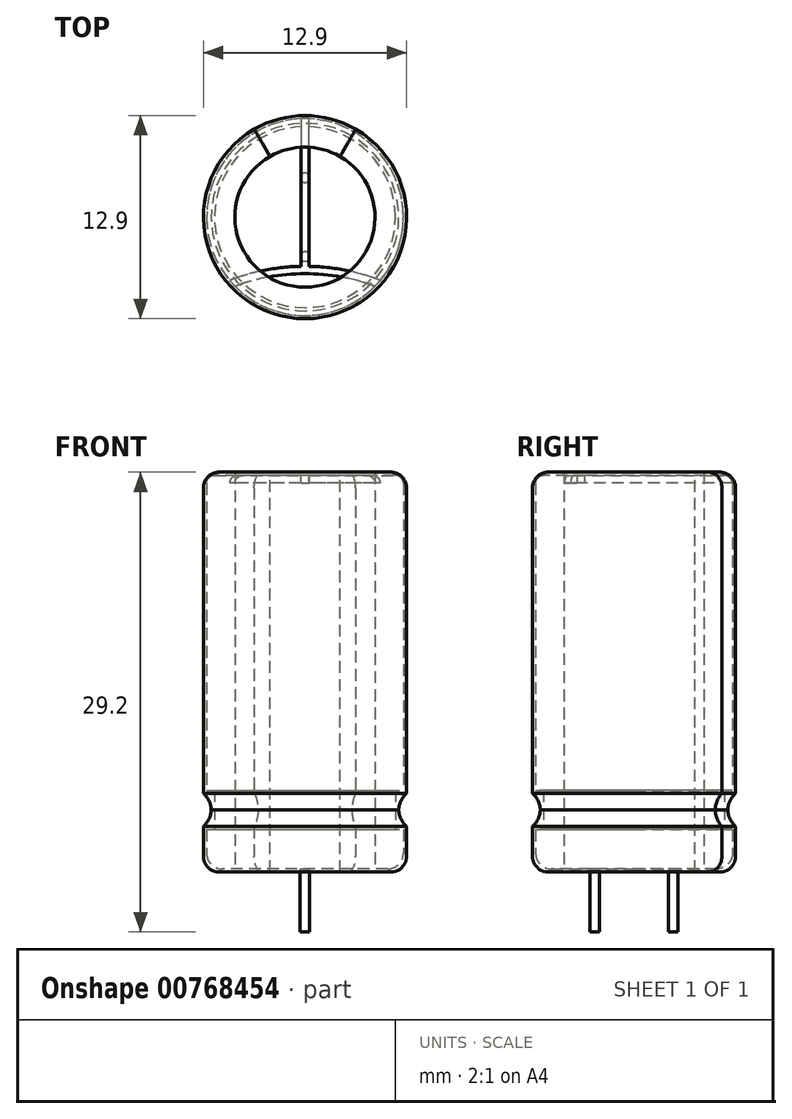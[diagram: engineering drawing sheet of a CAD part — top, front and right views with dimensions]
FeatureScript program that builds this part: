
annotation { "Feature Type Name" : "Feature", "Feature Type Description" : "" }
export const myFeature = defineFeature(function(context is Context, id is Id, definition is map)
    precondition{}
    {
        {
            var Q0;
            Q0=qCreatedBy(makeId("Front.planeOp"),FACE);
            var sketch = newSketch(context, id + "F0", { "sketchPlane" : qUnion([Q0])});
            skLineSegment(sketch, "E0", {"start": v(0, 0) * mm, "end": v(0, 25) * mm});
            skLineSegment(sketch, "E1", {"start": v(0, 25) * mm, "end": v(6.25, 25) * mm});
            skLineSegment(sketch, "E2", {"start": v(6.25, 25) * mm, "end": v(6.25, 5) * mm});
            skLineSegment(sketch, "E3", {"start": v(6.25, 5) * mm, "end": v(5.75, 5) * mm});
            skLineSegment(sketch, "E4", {"start": v(5.75, 5) * mm, "end": v(5.75, 2.5) * mm});
            skLineSegment(sketch, "E5", {"start": v(5.75, 2.5) * mm, "end": v(6.25, 2.5) * mm});
            skLineSegment(sketch, "E6", {"start": v(6.25, 2.5) * mm, "end": v(6.25, 0) * mm});
            skLineSegment(sketch, "E7", {"start": v(6.25, 0) * mm, "end": v(0, 0) * mm});
            skSolve(sketch);
        }
        {
            var Q0;
            Q0=makeQuery(id+"F0.imprint","IMPRINT",FACE,{"disambiguationData":[TD([[makeQuery(id+"F0.imprint","IMPRINT",EDGE,{"derivedFrom":sQuery(id+"F0.wireOp",EDGE,"E0")}),-1.0]])]});
            var Q1;
            Q1=sQuery(id+"F0.wireOp",EDGE,"E0");
            revolve(context, id + "F1", {"surfaceOperationType" : NewSurfaceOperationType.NEW, "entities" : qUnion([Q0]), "axis" : qUnion([Q1]), "revolveType" : RevolveType.FULL});
        }
        {
            var Q0;
            Q0=makeQuery(id+"F1.opRevolve","SWEPT_FACE",FACE,{"disambiguationData":[OSD([sQuery(id+"F0.wireOp",EDGE,"E1")])]});
            var sketch = newSketch(context, id + "F2", { "sketchPlane" : qUnion([Q0])});
            skLineSegment(sketch, "E8", {"start": v(0, 0) * mm, "end": v(-4.79, -4.02) * mm, "construction": true});
            skLineSegment(sketch, "E9", {"start": v(0, 0) * mm, "end": v(4.79, -4.02) * mm, "construction": true});
            skArc(sketch, "E10", {"start": v(4.79, -4.02) * mm, "mid": v(0, -3.12) * mm, "end": v(-4.79, -4.02) * mm});
            skLineSegment(sketch, "E11", {"start": v(-0.25, 6.24) * mm, "end": v(-0.25, -3.13) * mm});
            skLineSegment(sketch, "E12", {"start": v(0.25, -3.13) * mm, "end": v(0.25, 6.24) * mm});
            skArc(sketch, "E13", {"start": v(4.45, -4.39) * mm, "mid": v(0, -3.59) * mm, "end": v(-4.45, -4.39) * mm});
            skSolve(sketch);
        }
        {
            var Q0;
            {var subQ0=sQuery(id+"F2.wireOp",EDGE,"E11");Q0=makeQuery(id+"F2.imprint","IMPRINT",FACE,{"disambiguationData":[TD([[makeQuery(id+"F2.imprint","IMPRINT",EDGE,{"derivedFrom":subQ0}),1.0]])]});}
            var Q1;
            {var subQ5=sQuery(id+"F2.wireOp",EDGE,"E13");Q1=makeQuery(id+"F2.imprint","IMPRINT",FACE,{"disambiguationData":[TD([[makeQuery(id+"F2.imprint","IMPRINT",EDGE,{"derivedFrom":subQ5}),-1.0]])]});}
            extrude(context, id + "F3", {"entities" : qUnion([Q0, Q1]), "operationType" : NewBodyOperationType.REMOVE, "oppositeDirection" : true, "depth" : 0.5 * mm, "offsetDistance" : 25 * mm});
        }
        {
            var Q0;
            {var subQ0=sQuery(id+"F0.wireOp",EDGE,"E1");var subQ1=sQuery(id+"F0.wireOp",EDGE,"E2");var subQ3=makeQuery(id+"F1.opRevolve","SWEPT_EDGE",EDGE,{"disambiguationData":[OSD([subQ0,subQ1])]});var subQ4=sQuery(id+"F2.wireOp",EDGE,"E11");Q0=makeQuery(id+"F3.boolean.opBoolean","SPLIT",EDGE,{"disambiguationData":[TD([makeQuery(id+"F3.opExtrude","SWEPT_FACE",FACE,{"disambiguationData":[OSD([subQ4])]})])],"derivedFrom":subQ3});}
            var Q1;
            {var subQ0=sQuery(id+"F0.wireOp",EDGE,"E1");var subQ1=sQuery(id+"F0.wireOp",EDGE,"E2");Q1=makeQuery(id+"F3.boolean.opBoolean","SPLIT",EDGE,{"disambiguationData":[TD([makeQuery(id+"F3.opExtrude","SWEPT_FACE",FACE,{"disambiguationData":[OSD([sQuery(id+"F2.wireOp",EDGE,"E13")])]})])],"derivedFrom":makeQuery(id+"F1.opRevolve","SWEPT_EDGE",EDGE,{"disambiguationData":[OSD([subQ0,subQ1])]})});}
            var Q2;
            {var subQ0=sQuery(id+"F0.wireOp",EDGE,"E1");var subQ1=sQuery(id+"F0.wireOp",EDGE,"E2");var subQ3=makeQuery(id+"F1.opRevolve","SWEPT_EDGE",EDGE,{"disambiguationData":[OSD([subQ0,subQ1])]});var subQ4=sQuery(id+"F2.wireOp",EDGE,"E12");Q2=makeQuery(id+"F3.boolean.opBoolean","SPLIT",EDGE,{"disambiguationData":[TD([makeQuery(id+"F3.opExtrude","SWEPT_FACE",FACE,{"disambiguationData":[OSD([subQ4])]})])],"derivedFrom":subQ3});}
            fillet(context, id + "F4", {"entities" : qUnion([Q0, Q1, Q2]), "radius" : 0.5 * mm, "tangentPropagation" : true, "allowEdgeOverflow" : false});
        }
        {
            var Q0;
            Q0=makeQuery(id+"F1.opRevolve","SWEPT_EDGE",EDGE,{"disambiguationData":[OSD([sQuery(id+"F0.wireOp",EDGE,"E6"),sQuery(id+"F0.wireOp",EDGE,"E7")])]});
            fillet(context, id + "F5", {"entities" : qUnion([Q0]), "radius" : 1 * mm, "tangentPropagation" : true, "allowEdgeOverflow" : false});
        }
        {
            var Q0;
            Q0=qCreatedBy(makeId("Front.planeOp"),FACE);
            var sketch = newSketch(context, id + "F6", { "sketchPlane" : qUnion([Q0])});
            skLineSegment(sketch, "E14.0", {"start": v(6.25, 0) * mm, "end": v(0, 0) * mm, "construction": true});
            skLineSegment(sketch, "E15.0", {"start": v(6.25, 2.5) * mm, "end": v(6.25, 0) * mm, "construction": true});
            skLineSegment(sketch, "E16.0", {"start": v(5.75, 2.5) * mm, "end": v(6.25, 2.5) * mm, "construction": true});
            skLineSegment(sketch, "E17", {"start": v(5.75, 5) * mm, "end": v(5.75, 2.5) * mm, "construction": true});
            skLineSegment(sketch, "E18.0", {"start": v(6.25, 5) * mm, "end": v(5.75, 5) * mm, "construction": true});
            skLineSegment(sketch, "E19.0", {"start": v(6.25, 25) * mm, "end": v(6.25, 5) * mm, "construction": true});
            skLineSegment(sketch, "E20.0", {"start": v(6.45, 2.7) * mm, "end": v(6.45, 0) * mm});
            skLineSegment(sketch, "E20.1", {"start": v(6.45, 25) * mm, "end": v(6.45, 4.8) * mm});
            skLineSegment(sketch, "E20.2", {"start": v(6.45, 4.8) * mm, "end": v(5.95, 4.8) * mm});
            skLineSegment(sketch, "E20.3", {"start": v(5.95, 4.8) * mm, "end": v(5.95, 2.7) * mm});
            skLineSegment(sketch, "E20.4", {"start": v(5.95, 2.7) * mm, "end": v(6.45, 2.7) * mm});
            skLineSegment(sketch, "E21", {"start": v(6.45, 0) * mm, "end": v(6.45, -0.2) * mm});
            skLineSegment(sketch, "E22", {"start": v(6.45, -0.2) * mm, "end": v(4.45, -0.2) * mm});
            skLineSegment(sketch, "E23", {"start": v(4.45, -0.2) * mm, "end": v(4.45, 25.2) * mm});
            skLineSegment(sketch, "E24", {"start": v(4.45, 25.2) * mm, "end": v(6.45, 25.2) * mm});
            skLineSegment(sketch, "E25", {"start": v(6.45, 25.2) * mm, "end": v(6.45, 25) * mm});
            skSolve(sketch);
        }
        {
            var Q0;
            Q0=makeQuery(id+"F6.imprint","IMPRINT",FACE,{"disambiguationData":[TD([[makeQuery(id+"F6.imprint","IMPRINT",EDGE,{"derivedFrom":sQuery(id+"F6.wireOp",EDGE,"E20.0")}),-1.0]])]});
            var Q1;
            Q1=sQuery(id+"F0.wireOp",EDGE,"E0");
            revolve(context, id + "F7", {"surfaceOperationType" : NewSurfaceOperationType.NEW, "entities" : qUnion([Q0]), "axis" : qUnion([Q1]), "revolveType" : RevolveType.TWO_DIRECTIONS, "angle" : 60 * degree, "angleBack" : 120 * degree});
        }
        {
            var Q0;
            Q0=makeQuery(id+"F6.imprint","IMPRINT",FACE,{"disambiguationData":[TD([[makeQuery(id+"F6.imprint","IMPRINT",EDGE,{"derivedFrom":sQuery(id+"F6.wireOp",EDGE,"E20.0")}),-1.0]])]});
            var Q1;
            Q1=sQuery(id+"F0.wireOp",EDGE,"E0");
            revolve(context, id + "F8", {"surfaceOperationType" : NewSurfaceOperationType.NEW, "entities" : qUnion([Q0]), "axis" : qUnion([Q1]), "revolveType" : RevolveType.TWO_DIRECTIONS, "angle" : 120 * degree, "angleBack" : 60 * degree});
        }
        {
            var Q0;
            Q0=makeQuery(id+"F7.opRevolve","SWEPT_EDGE",EDGE,{"disambiguationData":[OSD([sQuery(id+"F6.wireOp",EDGE,"E24"),sQuery(id+"F6.wireOp",EDGE,"E25")])]});
            var Q1;
            Q1=makeQuery(id+"F8.opRevolve","SWEPT_EDGE",EDGE,{"disambiguationData":[OSD([sQuery(id+"F6.wireOp",EDGE,"E24"),sQuery(id+"F6.wireOp",EDGE,"E25")])]});
            var Q2;
            Q2=makeQuery(id+"F7.opRevolve","SWEPT_EDGE",EDGE,{"disambiguationData":[OSD([sQuery(id+"F6.wireOp",EDGE,"E21"),sQuery(id+"F6.wireOp",EDGE,"E22")])]});
            var Q3;
            Q3=makeQuery(id+"F8.opRevolve","SWEPT_EDGE",EDGE,{"disambiguationData":[OSD([sQuery(id+"F6.wireOp",EDGE,"E21"),sQuery(id+"F6.wireOp",EDGE,"E22")])]});
            fillet(context, id + "F9", {"entities" : qUnion([Q0, Q1, Q2, Q3]), "radius" : 1 * mm, "tangentPropagation" : true, "allowEdgeOverflow" : false});
        }
        {
            var Q0;
            Q0=makeQuery(id+"F7.opRevolve","SWEPT_EDGE",EDGE,{"disambiguationData":[OSD([sQuery(id+"F6.wireOp",EDGE,"E20.3"),sQuery(id+"F6.wireOp",EDGE,"E20.4")])]});
            var Q1;
            Q1=makeQuery(id+"F8.opRevolve","SWEPT_EDGE",EDGE,{"disambiguationData":[OSD([sQuery(id+"F6.wireOp",EDGE,"E20.3"),sQuery(id+"F6.wireOp",EDGE,"E20.4")])]});
            var Q2;
            Q2=makeQuery(id+"F7.opRevolve","SWEPT_EDGE",EDGE,{"disambiguationData":[OSD([sQuery(id+"F6.wireOp",EDGE,"E20.2"),sQuery(id+"F6.wireOp",EDGE,"E20.3")])]});
            var Q3;
            Q3=makeQuery(id+"F8.opRevolve","SWEPT_EDGE",EDGE,{"disambiguationData":[OSD([sQuery(id+"F6.wireOp",EDGE,"E20.2"),sQuery(id+"F6.wireOp",EDGE,"E20.3")])]});
            fillet(context, id + "F10", {"entities" : qUnion([Q0, Q1, Q2, Q3]), "radius" : 1.5 * mm, "tangentPropagation" : true, "allowEdgeOverflow" : false});
        }
        {
            var Q0;
            Q0=qCreatedBy(makeId("Top.planeOp"),FACE);
            var sketch = newSketch(context, id + "F11", { "sketchPlane" : qUnion([Q0])});
            skCircle(sketch, "E26", {"center": v(0, 2.5) * mm, "radius": 0.3 * mm});
            skSolve(sketch);
        }
        {
            var Q0;
            Q0=qCreatedBy(makeId("Right.planeOp"),FACE);
            var sketch = newSketch(context, id + "F12", { "sketchPlane" : qUnion([Q0])});
            skLineSegment(sketch, "E27", {"start": v(2.5, 0) * mm, "end": v(2.5, -4) * mm});
            skSolve(sketch);
        }
        {
            var Q0;
            Q0=makeQuery(id+"F11.imprint","IMPRINT",FACE,{"disambiguationData":[TD([[makeQuery(id+"F11.imprint","IMPRINT",EDGE,{"derivedFrom":sQuery(id+"F11.wireOp",EDGE,"E26")}),1.0]])]});
            var Q1;
            Q1=sQuery(id+"F11.wireOp",EDGE,"E26");
            var Q2;
            Q2=sQuery(id+"F12.wireOp",EDGE,"E27");
            sweep(context, id + "F13", {"profiles" : qUnion([Q0]), "surfaceProfiles" : qUnion([Q1]), "path" : qUnion([Q2])});
        }
        {
            var Q0;
            Q0=makeQuery(id+"F13.opSweep","SWEPT_BODY",BODY,{"disambiguationData":[OSD([sQuery(id+"F11.wireOp",EDGE,"E26"),sQuery(id+"F12.wireOp",EDGE,"E27")])]});
            var Q1;
            Q1=sQuery(id+"F0.wireOp",EDGE,"E0");
            circularPattern(context, id + "F14", {"entities" : qUnion([Q0]), "axis" : qUnion([Q1]), "angle" : 360 * degree, "instanceCount" : 2, "equalSpace" : true});
        }
    });
